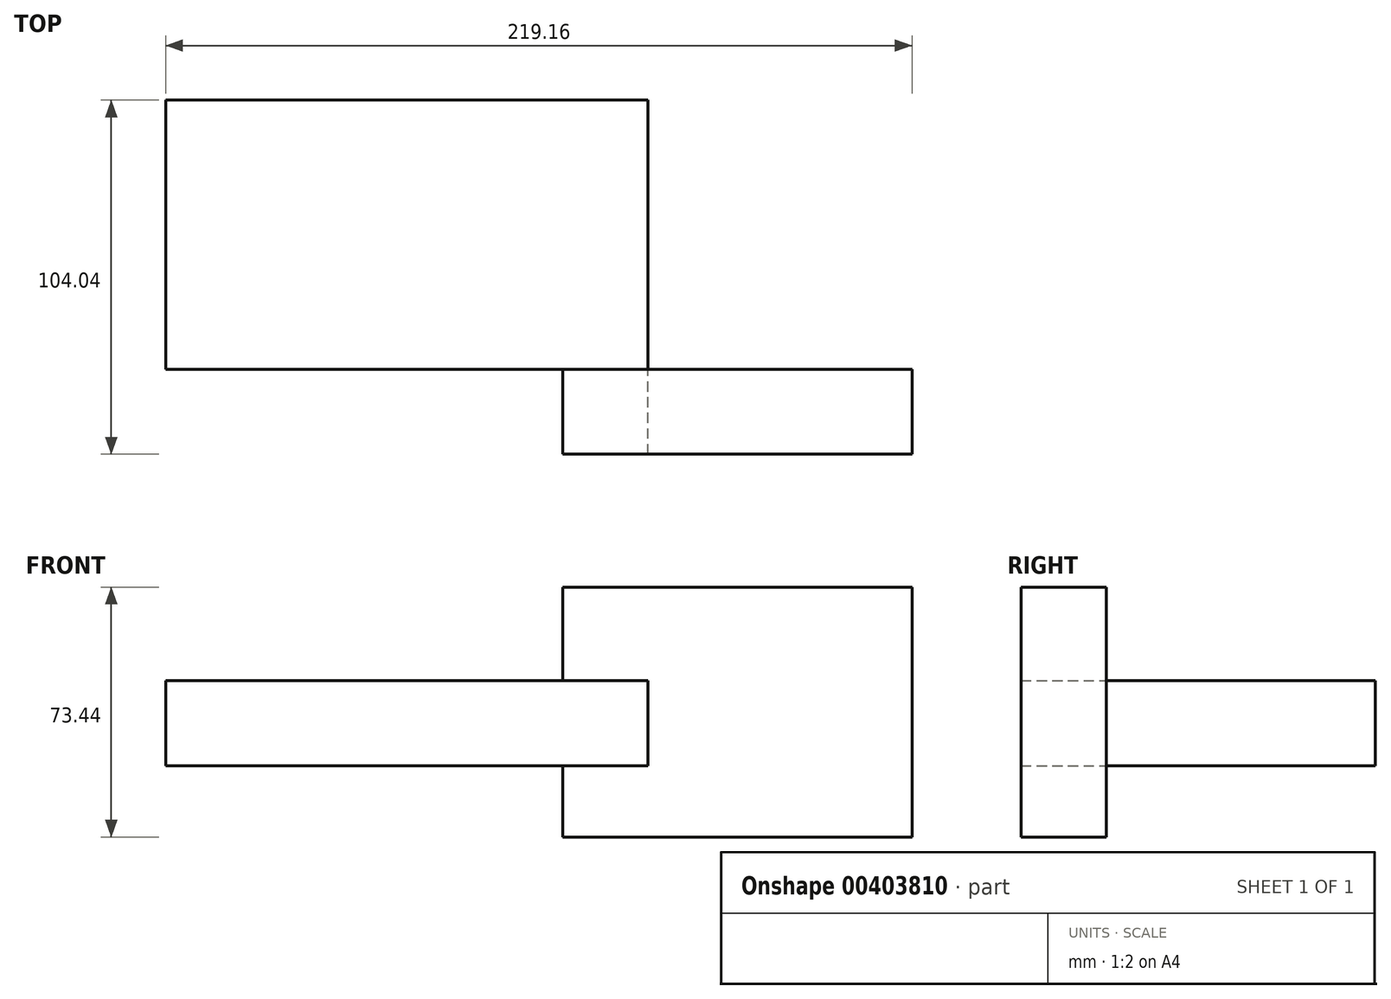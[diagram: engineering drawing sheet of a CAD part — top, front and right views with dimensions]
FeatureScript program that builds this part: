
annotation { "Feature Type Name" : "Feature", "Feature Type Description" : "" }
export const myFeature = defineFeature(function(context is Context, id is Id, definition is map)
    precondition{}
    {
        {
            var Q0;
            Q0=qCreatedBy(makeId("Top.planeOp"),FACE);
            var sketch = newSketch(context, id + "F0", { "sketchPlane" : qUnion([Q0])});
            skLineSegment(sketch, "E0.bottom", {"start": v(-90.44, -23.41) * mm, "end": v(51.14, -23.41) * mm});
            skLineSegment(sketch, "E0.top", {"start": v(-90.44, 55.63) * mm, "end": v(51.14, 55.63) * mm});
            skLineSegment(sketch, "E0.left", {"start": v(-90.44, -23.41) * mm, "end": v(-90.44, 55.63) * mm});
            skLineSegment(sketch, "E0.right", {"start": v(51.14, -23.41) * mm, "end": v(51.14, 55.63) * mm});
            skLineSegment(sketch, "E1.bottom", {"start": v(51.14, -23.41) * mm, "end": v(82.91, -23.41) * mm});
            skLineSegment(sketch, "E1.top", {"start": v(51.14, -66.44) * mm, "end": v(82.91, -66.44) * mm});
            skLineSegment(sketch, "E1.left", {"start": v(51.14, -23.41) * mm, "end": v(51.14, -66.44) * mm});
            skLineSegment(sketch, "E1.right", {"start": v(82.91, -23.41) * mm, "end": v(82.91, -66.44) * mm});
            skSolve(sketch);
        }
        {
            var Q0;
            Q0=makeQuery(id+"F0.imprint","IMPRINT",FACE,{"disambiguationData":[TD([[makeQuery(id+"F0.imprint","IMPRINT",EDGE,{"derivedFrom":sQuery(id+"F0.wireOp",EDGE,"E0.bottom")}),1.0]])]});
            extrude(context, id + "F1", {"entities" : qUnion([Q0]), "depth" : 25 * mm});
        }
        {
            var Q0;
            Q0=makeQuery(id+"F1.opExtrude","SWEPT_FACE",FACE,{"disambiguationData":[OSD([sQuery(id+"F0.wireOp",EDGE,"E0.bottom")])]});
            var sketch = newSketch(context, id + "F2", { "sketchPlane" : qUnion([Q0])});
            skLineSegment(sketch, "E2.bottom", {"start": v(26.12, 52.55) * mm, "end": v(128.72, 52.55) * mm});
            skLineSegment(sketch, "E2.top", {"start": v(26.12, -20.89) * mm, "end": v(128.72, -20.89) * mm});
            skLineSegment(sketch, "E2.left", {"start": v(26.12, 52.55) * mm, "end": v(26.12, -20.89) * mm});
            skLineSegment(sketch, "E2.right", {"start": v(128.72, 52.55) * mm, "end": v(128.72, -20.89) * mm});
            skSolve(sketch);
        }
        {
            var Q0;
            {var subQ5=sQuery(id+"F2.wireOp",EDGE,"E2.bottom");Q0=makeQuery(id+"F2.imprint","IMPRINT",FACE,{"disambiguationData":[TD([[makeQuery(id+"F2.imprint","IMPRINT",EDGE,{"derivedFrom":subQ5}),-1.0]])]});}
            extrude(context, id + "F3", {"entities" : qUnion([Q0]), "depth" : 25 * mm});
        }
    });
